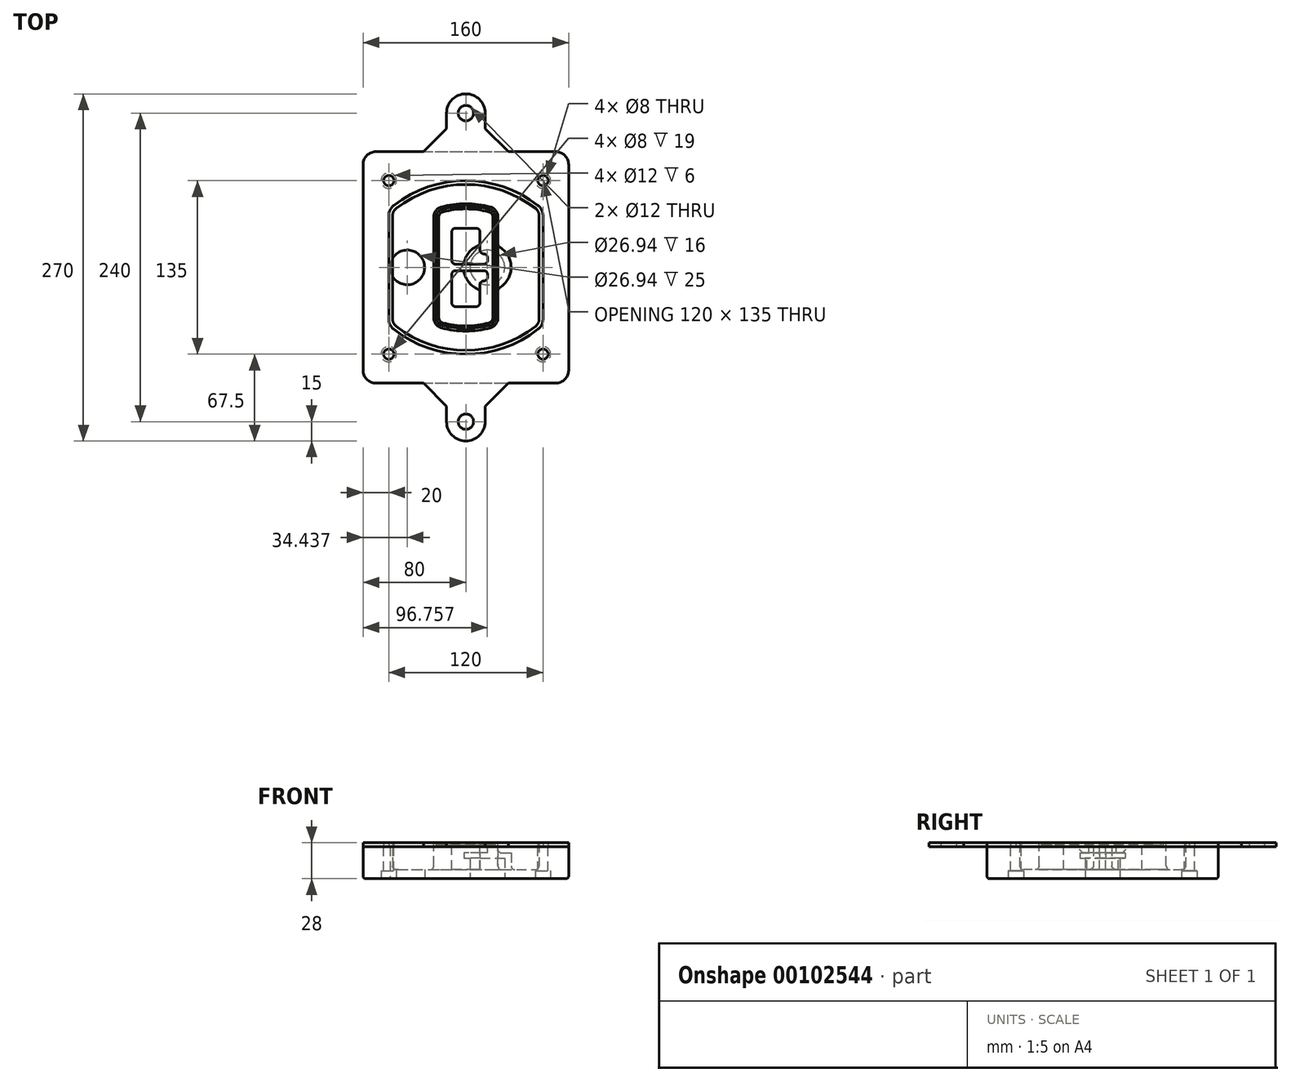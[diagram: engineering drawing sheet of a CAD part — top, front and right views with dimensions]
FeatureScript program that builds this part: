
annotation { "Feature Type Name" : "Feature", "Feature Type Description" : "" }
export const myFeature = defineFeature(function(context is Context, id is Id, definition is map)
    precondition{}
    {
        {
            var Q0;
            Q0=qCreatedBy(makeId("Top.planeOp"),FACE);
            var sketch = newSketch(context, id + "F0", { "sketchPlane" : qUnion([Q0])});
            skPoint(sketch, "E0.rect.middle", {"position": v(0, 0) * mm});
            skLineSegment(sketch, "E1.bottom", {"start": v(-70, -90) * mm, "end": v(70, -90) * mm});
            skLineSegment(sketch, "E1.top", {"start": v(-70, 90) * mm, "end": v(70, 90) * mm});
            skLineSegment(sketch, "E1.left", {"start": v(-80, -80) * mm, "end": v(-80, 80) * mm});
            skLineSegment(sketch, "E1.right", {"start": v(80, -80) * mm, "end": v(80, 80) * mm});
            skLineSegment(sketch, "E2", {"start": v(-80, 90) * mm, "end": v(80, -90) * mm, "construction": true});
            skLineSegment(sketch, "E3", {"start": v(80, 90) * mm, "end": v(-80, -90) * mm, "construction": true});
            skCircle(sketch, "E4", {"center": v(-60, 67.5) * mm, "radius": 4 * mm});
            skCircle(sketch, "E5", {"center": v(60, 67.5) * mm, "radius": 4 * mm});
            skCircle(sketch, "E6", {"center": v(60, -67.5) * mm, "radius": 4 * mm});
            skCircle(sketch, "E7", {"center": v(-60, -67.5) * mm, "radius": 4 * mm});
            skLineSegment(sketch, "E8", {"start": v(-60, 67.5) * mm, "end": v(60, 67.5) * mm, "construction": true});
            skLineSegment(sketch, "E9", {"start": v(60, 67.5) * mm, "end": v(60, -67.5) * mm, "construction": true});
            skLineSegment(sketch, "E10", {"start": v(60, -67.5) * mm, "end": v(-60, -67.5) * mm, "construction": true});
            skLineSegment(sketch, "E11", {"start": v(-60, -67.5) * mm, "end": v(-60, 67.5) * mm, "construction": true});
            skLineSegment(sketch, "E12", {"start": v(-60, 40.3) * mm, "end": v(-60, -40.3) * mm});
            skLineSegment(sketch, "E13", {"start": v(60, 40.3) * mm, "end": v(60, -40.3) * mm});
            skArc(sketch, "E14", {"start": v(56.15, 48.18) * mm, "mid": v(0, 67.5) * mm, "end": v(-56.15, 48.18) * mm});
            skArc(sketch, "E15", {"start": v(-56.15, -48.18) * mm, "mid": v(0, -67.5) * mm, "end": v(56.15, -48.18) * mm});
            skLineSegment(sketch, "E16", {"start": v(-60, 0) * mm, "end": v(60, 0) * mm, "construction": true});
            skPoint(sketch, "E17.visualSharp", {"position": v(-60, -45) * mm});
            skArc(sketch, "E17.filletArc", {"start": v(-60, -40.3) * mm, "mid": v(-58.99, -44.68) * mm, "end": v(-56.15, -48.18) * mm});
            skPoint(sketch, "E18.visualSharp", {"position": v(-60, 45) * mm});
            skArc(sketch, "E18.filletArc", {"start": v(-56.15, 48.18) * mm, "mid": v(-58.99, 44.68) * mm, "end": v(-60, 40.3) * mm});
            skPoint(sketch, "E19.visualSharp", {"position": v(60, 45) * mm});
            skArc(sketch, "E19.filletArc", {"start": v(60, 40.3) * mm, "mid": v(58.99, 44.68) * mm, "end": v(56.15, 48.18) * mm});
            skPoint(sketch, "E20.visualSharp", {"position": v(60, -45) * mm});
            skArc(sketch, "E20.filletArc", {"start": v(56.15, -48.18) * mm, "mid": v(58.99, -44.68) * mm, "end": v(60, -40.3) * mm});
            skPoint(sketch, "E21.visualSharp", {"position": v(-80, 90) * mm});
            skArc(sketch, "E21.filletArc", {"start": v(-70, 90) * mm, "mid": v(-77.07, 87.07) * mm, "end": v(-80, 80) * mm});
            skPoint(sketch, "E22.visualSharp", {"position": v(80, 90) * mm});
            skArc(sketch, "E22.filletArc", {"start": v(80, 80) * mm, "mid": v(77.07, 87.07) * mm, "end": v(70, 90) * mm});
            skPoint(sketch, "E23.visualSharp", {"position": v(80, -90) * mm});
            skArc(sketch, "E23.filletArc", {"start": v(70, -90) * mm, "mid": v(77.07, -87.07) * mm, "end": v(80, -80) * mm});
            skPoint(sketch, "E24.visualSharp", {"position": v(-80, -90) * mm});
            skArc(sketch, "E24.filletArc", {"start": v(-80, -80) * mm, "mid": v(-77.07, -87.07) * mm, "end": v(-70, -90) * mm});
            skArc(sketch, "E25.0", {"start": v(57, 40.3) * mm, "mid": v(56.3, 43.36) * mm, "end": v(54.3, 45.81) * mm});
            skLineSegment(sketch, "E25.1", {"start": v(57, 40.3) * mm, "end": v(57, -40.3) * mm});
            skArc(sketch, "E25.2", {"start": v(54.3, -45.81) * mm, "mid": v(56.3, -43.36) * mm, "end": v(57, -40.3) * mm});
            skArc(sketch, "E25.3", {"start": v(-54.3, -45.81) * mm, "mid": v(0, -64.5) * mm, "end": v(54.3, -45.81) * mm});
            skArc(sketch, "E25.4", {"start": v(-57, -40.3) * mm, "mid": v(-56.3, -43.36) * mm, "end": v(-54.3, -45.81) * mm});
            skArc(sketch, "E25.5", {"start": v(54.3, 45.81) * mm, "mid": v(0, 64.5) * mm, "end": v(-54.3, 45.81) * mm});
            skLineSegment(sketch, "E25.6", {"start": v(-57, 40.3) * mm, "end": v(-57, -40.3) * mm});
            skArc(sketch, "E25.7", {"start": v(-54.3, 45.81) * mm, "mid": v(-56.3, 43.36) * mm, "end": v(-57, 40.3) * mm});
            skArc(sketch, "E26.0", {"start": v(-58.62, 51.33) * mm, "mid": v(-62.58, 46.43) * mm, "end": v(-64, 40.3) * mm});
            skArc(sketch, "E26.1", {"start": v(58.62, 51.33) * mm, "mid": v(0, 71.5) * mm, "end": v(-58.62, 51.33) * mm});
            skArc(sketch, "E26.2", {"start": v(64, 40.3) * mm, "mid": v(62.58, 46.43) * mm, "end": v(58.62, 51.33) * mm});
            skLineSegment(sketch, "E26.3", {"start": v(64, 40.3) * mm, "end": v(64, -40.3) * mm});
            skArc(sketch, "E26.4", {"start": v(58.62, -51.33) * mm, "mid": v(62.58, -46.43) * mm, "end": v(64, -40.3) * mm});
            skLineSegment(sketch, "E26.5", {"start": v(-64, 40.3) * mm, "end": v(-64, -40.3) * mm});
            skArc(sketch, "E26.6", {"start": v(-58.62, -51.33) * mm, "mid": v(0, -71.5) * mm, "end": v(58.62, -51.33) * mm});
            skArc(sketch, "E26.7", {"start": v(-64, -40.3) * mm, "mid": v(-62.58, -46.43) * mm, "end": v(-58.62, -51.33) * mm});
            skSolve(sketch);
        }
        {
            var Q0;
            Q0=makeQuery(id+"F0.imprint","IMPRINT",FACE,{"disambiguationData":[TD([[makeQuery(id+"F0.imprint","IMPRINT",EDGE,{"derivedFrom":sQuery(id+"F0.wireOp",EDGE,"E1.bottom")}),1.0]])]});
            var Q1;
            Q1=makeQuery(id+"F0.imprint","IMPRINT",FACE,{"disambiguationData":[TD([[makeQuery(id+"F0.imprint","IMPRINT",EDGE,{"derivedFrom":sQuery(id+"F0.wireOp",EDGE,"E12")}),1.0]])]});
            var Q2;
            Q2=makeQuery(id+"F0.imprint","IMPRINT",FACE,{"disambiguationData":[TD([[makeQuery(id+"F0.imprint","IMPRINT",EDGE,{"derivedFrom":sQuery(id+"F0.wireOp",EDGE,"E25.0")}),1.0]])]});
            var Q3;
            Q3=makeQuery(id+"F0.imprint","IMPRINT",FACE,{"disambiguationData":[TD([[makeQuery(id+"F0.imprint","IMPRINT",EDGE,{"derivedFrom":sQuery(id+"F0.wireOp",EDGE,"E12")}),-1.0]])]});
            extrude(context, id + "F1", {"entities" : qUnion([Q0, Q1, Q2, Q3]), "oppositeDirection" : true, "depth" : 25 * mm});
        }
        {
            var Q0;
            Q0=makeQuery(id+"F0.imprint","IMPRINT",FACE,{"disambiguationData":[TD([[makeQuery(id+"F0.imprint","IMPRINT",EDGE,{"derivedFrom":sQuery(id+"F0.wireOp",EDGE,"E12")}),1.0]])]});
            extrude(context, id + "F2", {"entities" : qUnion([Q0]), "operationType" : NewBodyOperationType.ADD, "depth" : 3 * mm});
        }
        {
            var Q0;
            Q0=makeQuery(id+"F0.imprint","IMPRINT",FACE,{"disambiguationData":[TD([[makeQuery(id+"F0.imprint","IMPRINT",EDGE,{"derivedFrom":sQuery(id+"F0.wireOp",EDGE,"E25.0")}),1.0]])]});
            extrude(context, id + "F3", {"entities" : qUnion([Q0]), "operationType" : NewBodyOperationType.REMOVE, "oppositeDirection" : true, "depth" : 18 * mm});
        }
        {
            var Q0;
            Q0=makeQuery(id+"F2.opExtrude","CAP_FACE",FACE,{"disambiguationData":[OSD([sQuery(id+"F0.wireOp",EDGE,"E12"),sQuery(id+"F0.wireOp",EDGE,"E13"),sQuery(id+"F0.wireOp",EDGE,"E14"),sQuery(id+"F0.wireOp",EDGE,"E15"),sQuery(id+"F0.wireOp",EDGE,"E17.filletArc"),sQuery(id+"F0.wireOp",EDGE,"E18.filletArc"),sQuery(id+"F0.wireOp",EDGE,"E19.filletArc"),sQuery(id+"F0.wireOp",EDGE,"E20.filletArc"),sQuery(id+"F0.wireOp",EDGE,"E25.0"),sQuery(id+"F0.wireOp",EDGE,"E25.1"),sQuery(id+"F0.wireOp",EDGE,"E25.2"),sQuery(id+"F0.wireOp",EDGE,"E25.3"),sQuery(id+"F0.wireOp",EDGE,"E25.4"),sQuery(id+"F0.wireOp",EDGE,"E25.5"),sQuery(id+"F0.wireOp",EDGE,"E25.6"),sQuery(id+"F0.wireOp",EDGE,"E25.7")])],"isStart":false});
            var sketch = newSketch(context, id + "F4", { "sketchPlane" : qUnion([Q0])});
            skArc(sketch, "E27.0", {"start": v(-19.08, -46.97) * mm, "mid": v(0, -49.5) * mm, "end": v(19.08, -46.97) * mm});
            skArc(sketch, "E28.0", {"start": v(19.08, 46.97) * mm, "mid": v(0, 49.5) * mm, "end": v(-19.08, 46.97) * mm});
            skLineSegment(sketch, "E29", {"start": v(-25, 39.25) * mm, "end": v(-25, -39.25) * mm});
            skLineSegment(sketch, "E30", {"start": v(25, 39.25) * mm, "end": v(25, -39.25) * mm});
            skLineSegment(sketch, "E31", {"start": v(-25, 45.1) * mm, "end": v(25, 45.1) * mm, "construction": true});
            skLineSegment(sketch, "E32", {"start": v(-25, -45.1) * mm, "end": v(25, -45.1) * mm, "construction": true});
            skPoint(sketch, "E33.visualSharp", {"position": v(-25, 45.1) * mm});
            skArc(sketch, "E33.filletArc", {"start": v(-19.08, 46.97) * mm, "mid": v(-23.35, 44.11) * mm, "end": v(-25, 39.25) * mm});
            skPoint(sketch, "E34.visualSharp", {"position": v(25, 45.1) * mm});
            skArc(sketch, "E34.filletArc", {"start": v(25, 39.25) * mm, "mid": v(23.35, 44.11) * mm, "end": v(19.08, 46.97) * mm});
            skPoint(sketch, "E35.visualSharp", {"position": v(25, -45.1) * mm});
            skArc(sketch, "E35.filletArc", {"start": v(19.08, -46.97) * mm, "mid": v(23.35, -44.11) * mm, "end": v(25, -39.25) * mm});
            skPoint(sketch, "E36.visualSharp", {"position": v(-25, -45.1) * mm});
            skArc(sketch, "E36.filletArc", {"start": v(-25, -39.25) * mm, "mid": v(-23.35, -44.11) * mm, "end": v(-19.08, -46.97) * mm});
            skArc(sketch, "E37.0", {"start": v(54.3, 45.81) * mm, "mid": v(0, 64.5) * mm, "end": v(-54.3, 45.81) * mm});
            skArc(sketch, "E37.1", {"start": v(-54.3, 45.81) * mm, "mid": v(-56.3, 43.36) * mm, "end": v(-57, 40.3) * mm});
            skLineSegment(sketch, "E37.2", {"start": v(-57, 40.3) * mm, "end": v(-57, -40.3) * mm});
            skArc(sketch, "E37.3", {"start": v(-57, -40.3) * mm, "mid": v(-56.3, -43.36) * mm, "end": v(-54.3, -45.81) * mm});
            skArc(sketch, "E37.4", {"start": v(-54.3, -45.81) * mm, "mid": v(0, -64.5) * mm, "end": v(54.3, -45.81) * mm});
            skArc(sketch, "E37.5", {"start": v(54.3, -45.81) * mm, "mid": v(56.3, -43.36) * mm, "end": v(57, -40.3) * mm});
            skLineSegment(sketch, "E37.6", {"start": v(57, 40.3) * mm, "end": v(57, -40.3) * mm});
            skArc(sketch, "E37.7", {"start": v(57, 40.3) * mm, "mid": v(56.3, 43.36) * mm, "end": v(54.3, 45.81) * mm});
            skLineSegment(sketch, "E38.0", {"start": v(23, 39.25) * mm, "end": v(23, -39.25) * mm});
            skArc(sketch, "E38.1", {"start": v(18.56, -45.04) * mm, "mid": v(21.76, -42.9) * mm, "end": v(23, -39.25) * mm});
            skArc(sketch, "E38.2", {"start": v(-18.56, -45.04) * mm, "mid": v(0, -47.5) * mm, "end": v(18.56, -45.04) * mm});
            skArc(sketch, "E38.3", {"start": v(-23, -39.25) * mm, "mid": v(-21.76, -42.9) * mm, "end": v(-18.56, -45.04) * mm});
            skLineSegment(sketch, "E38.4", {"start": v(-23, 39.25) * mm, "end": v(-23, -39.25) * mm});
            skArc(sketch, "E38.5", {"start": v(23, 39.25) * mm, "mid": v(21.76, 42.9) * mm, "end": v(18.56, 45.04) * mm});
            skArc(sketch, "E38.6", {"start": v(-18.56, 45.04) * mm, "mid": v(-21.76, 42.9) * mm, "end": v(-23, 39.25) * mm});
            skArc(sketch, "E38.7", {"start": v(18.56, 45.04) * mm, "mid": v(0, 47.5) * mm, "end": v(-18.56, 45.04) * mm});
            skArc(sketch, "E39.0", {"start": v(21, 39.25) * mm, "mid": v(20.18, 41.68) * mm, "end": v(18.04, 43.1) * mm});
            skLineSegment(sketch, "E39.1", {"start": v(21, 39.25) * mm, "end": v(21, -39.25) * mm});
            skArc(sketch, "E39.2", {"start": v(18.04, -43.1) * mm, "mid": v(20.18, -41.68) * mm, "end": v(21, -39.25) * mm});
            skArc(sketch, "E39.3", {"start": v(-18.04, -43.1) * mm, "mid": v(0, -45.5) * mm, "end": v(18.04, -43.1) * mm});
            skArc(sketch, "E39.4", {"start": v(-21, -39.25) * mm, "mid": v(-20.18, -41.68) * mm, "end": v(-18.04, -43.1) * mm});
            skArc(sketch, "E39.5", {"start": v(18.04, 43.1) * mm, "mid": v(0, 45.5) * mm, "end": v(-18.04, 43.1) * mm});
            skLineSegment(sketch, "E39.6", {"start": v(-21, 39.25) * mm, "end": v(-21, -39.25) * mm});
            skArc(sketch, "E39.7", {"start": v(-18.04, 43.1) * mm, "mid": v(-20.18, 41.68) * mm, "end": v(-21, 39.25) * mm});
            skLineSegment(sketch, "E40", {"start": v(-25, 0) * mm, "end": v(25, 0) * mm, "construction": true});
            skLineSegment(sketch, "E41", {"start": v(-11, 5.5) * mm, "end": v(-11, 27.5) * mm});
            skLineSegment(sketch, "E42", {"start": v(-8, 30.5) * mm, "end": v(8, 30.5) * mm});
            skLineSegment(sketch, "E43", {"start": v(11, 27.5) * mm, "end": v(11, 13.5) * mm});
            skLineSegment(sketch, "E44", {"start": v(14, 10.5) * mm, "end": v(14, 10.5) * mm});
            skLineSegment(sketch, "E45", {"start": v(17, 7.5) * mm, "end": v(17, 5.5) * mm});
            skLineSegment(sketch, "E46", {"start": v(14, 2.5) * mm, "end": v(-8, 2.5) * mm});
            skPoint(sketch, "E47.visualSharp", {"position": v(-11, 30.5) * mm});
            skArc(sketch, "E47.filletArc", {"start": v(-8, 30.5) * mm, "mid": v(-10.12, 29.62) * mm, "end": v(-11, 27.5) * mm});
            skPoint(sketch, "E48.visualSharp", {"position": v(11, 30.5) * mm});
            skArc(sketch, "E48.filletArc", {"start": v(11, 27.5) * mm, "mid": v(10.12, 29.62) * mm, "end": v(8, 30.5) * mm});
            skPoint(sketch, "E49.visualSharp", {"position": v(11, 10.5) * mm});
            skArc(sketch, "E49.filletArc", {"start": v(11, 13.5) * mm, "mid": v(11.88, 11.38) * mm, "end": v(14, 10.5) * mm});
            skPoint(sketch, "E50.visualSharp", {"position": v(17, 10.5) * mm});
            skArc(sketch, "E50.filletArc", {"start": v(17, 7.5) * mm, "mid": v(16.12, 9.62) * mm, "end": v(14, 10.5) * mm});
            skPoint(sketch, "E51.visualSharp", {"position": v(17, 2.5) * mm});
            skArc(sketch, "E51.filletArc", {"start": v(14, 2.5) * mm, "mid": v(16.12, 3.38) * mm, "end": v(17, 5.5) * mm});
            skPoint(sketch, "E52.visualSharp", {"position": v(-11, 2.5) * mm});
            skArc(sketch, "E52.filletArc", {"start": v(-11, 5.5) * mm, "mid": v(-10.12, 3.38) * mm, "end": v(-8, 2.5) * mm});
            skLineSegment(sketch, "E53.0.MirrorCS", {"start": v(14, -2.5) * mm, "end": v(-8, -2.5) * mm});
            skArc(sketch, "E54.0.MirrorCS", {"start": v(-11, -5.5) * mm, "mid": v(-10.12, -3.38) * mm, "end": v(-8, -2.5) * mm});
            skLineSegment(sketch, "E55.0.MirrorCS", {"start": v(-11, -5.5) * mm, "end": v(-11, -27.5) * mm});
            skArc(sketch, "E56.0.MirrorCS", {"start": v(-8, -30.5) * mm, "mid": v(-10.12, -29.62) * mm, "end": v(-11, -27.5) * mm});
            skLineSegment(sketch, "E57.0.MirrorCS", {"start": v(-8, -30.5) * mm, "end": v(8, -30.5) * mm});
            skArc(sketch, "E58.0.MirrorCS", {"start": v(11, -27.5) * mm, "mid": v(10.12, -29.62) * mm, "end": v(8, -30.5) * mm});
            skLineSegment(sketch, "E59.0.MirrorCS", {"start": v(11, -27.5) * mm, "end": v(11, -13.5) * mm});
            skArc(sketch, "E60.0.MirrorCS", {"start": v(11, -13.5) * mm, "mid": v(11.88, -11.38) * mm, "end": v(14, -10.5) * mm});
            skArc(sketch, "E61.0.MirrorCS", {"start": v(17, -7.5) * mm, "mid": v(16.12, -9.62) * mm, "end": v(14, -10.5) * mm});
            skLineSegment(sketch, "E62.0.MirrorCS", {"start": v(17, -7.5) * mm, "end": v(17, -5.5) * mm});
            skArc(sketch, "E63.0.MirrorCS", {"start": v(14, -2.5) * mm, "mid": v(16.12, -3.38) * mm, "end": v(17, -5.5) * mm});
            skSolve(sketch);
        }
        {
            var Q0;
            Q0=makeQuery(id+"F4.imprint","IMPRINT",FACE,{"disambiguationData":[TD([[makeQuery(id+"F4.imprint","IMPRINT",EDGE,{"derivedFrom":sQuery(id+"F4.wireOp",EDGE,"E27.0")}),1.0]])]});
            var Q1;
            Q1=makeQuery(id+"F4.imprint","IMPRINT",FACE,{"disambiguationData":[TD([[makeQuery(id+"F4.imprint","IMPRINT",EDGE,{"derivedFrom":sQuery(id+"F4.wireOp",EDGE,"E38.0")}),-1.0]])]});
            var Q2;
            Q2=makeQuery(id+"F4.imprint","IMPRINT",FACE,{"disambiguationData":[TD([[makeQuery(id+"F4.imprint","IMPRINT",EDGE,{"derivedFrom":sQuery(id+"F4.wireOp",EDGE,"E39.0")}),1.0]])]});
            extrude(context, id + "F5", {"entities" : qUnion([Q0, Q1, Q2]), "operationType" : NewBodyOperationType.ADD, "endBound" : BoundingType.UP_TO_NEXT, "oppositeDirection" : true, "depth" : 25 * mm});
        }
        {
            var Q0;
            Q0=makeQuery(id+"F4.imprint","IMPRINT",FACE,{"disambiguationData":[TD([[makeQuery(id+"F4.imprint","IMPRINT",EDGE,{"derivedFrom":sQuery(id+"F4.wireOp",EDGE,"E38.0")}),-1.0]])]});
            extrude(context, id + "F6", {"entities" : qUnion([Q0]), "operationType" : NewBodyOperationType.REMOVE, "oppositeDirection" : true, "depth" : 2 * mm});
        }
        {
            var Q0;
            Q0=makeQuery(id+"F1.opExtrude","CAP_FACE",FACE,{"disambiguationData":[OSD([sQuery(id+"F0.wireOp",EDGE,"E1.bottom"),sQuery(id+"F0.wireOp",EDGE,"E1.top"),sQuery(id+"F0.wireOp",EDGE,"E1.left"),sQuery(id+"F0.wireOp",EDGE,"E1.right"),sQuery(id+"F0.wireOp",EDGE,"E4"),sQuery(id+"F0.wireOp",EDGE,"E5"),sQuery(id+"F0.wireOp",EDGE,"E6"),sQuery(id+"F0.wireOp",EDGE,"E7"),sQuery(id+"F0.wireOp",EDGE,"E21.filletArc"),sQuery(id+"F0.wireOp",EDGE,"E22.filletArc"),sQuery(id+"F0.wireOp",EDGE,"E23.filletArc"),sQuery(id+"F0.wireOp",EDGE,"E24.filletArc")])],"isStart":false});
            var sketch = newSketch(context, id + "F7", { "sketchPlane" : qUnion([Q0])});
            skCircle(sketch, "E64", {"center": v(16.76, 0) * mm, "radius": 13.47 * mm});
            skCircle(sketch, "E65", {"center": v(-45.56, 0) * mm, "radius": 13.47 * mm});
            skLineSegment(sketch, "E66", {"start": v(80, 0) * mm, "end": v(-80, 0) * mm});
            skCircle(sketch, "E67", {"center": v(16.76, 0) * mm, "radius": 18.47 * mm});
            skCircle(sketch, "E68", {"center": v(60, -67.5) * mm, "radius": 6 * mm});
            skCircle(sketch, "E69", {"center": v(-60, -67.5) * mm, "radius": 6 * mm});
            skCircle(sketch, "E70", {"center": v(-60, 67.5) * mm, "radius": 6 * mm});
            skCircle(sketch, "E71", {"center": v(60, 67.5) * mm, "radius": 6 * mm});
            skSolve(sketch);
        }
        {
            var Q0;
            {var subQ1=sQuery(id+"F7.wireOp",EDGE,"E66");var subQ4=sQuery(id+"F7.wireOp",EDGE,"E64");var subQ6=makeQuery(id+"F7.imprint","INTERSECT",VERTEX,{"disambiguationData":[OD(0.0)],"derivedFrom":[subQ4,subQ1]});Q0=makeQuery(id+"F7.imprint","IMPRINT",FACE,{"disambiguationData":[TD([[makeQuery(id+"F7.imprint","IMPRINT",EDGE,{"disambiguationData":[TD([[subQ6,-1.0]])],"derivedFrom":subQ4}),-1.0]])]});}
            var Q1;
            {var subQ0=sQuery(id+"F7.wireOp",EDGE,"E66");var subQ1=sQuery(id+"F7.wireOp",EDGE,"E64");var subQ3=makeQuery(id+"F7.imprint","INTERSECT",VERTEX,{"disambiguationData":[OD(0.0)],"derivedFrom":[subQ1,subQ0]});Q1=makeQuery(id+"F7.imprint","IMPRINT",FACE,{"disambiguationData":[TD([[makeQuery(id+"F7.imprint","IMPRINT",EDGE,{"disambiguationData":[TD([[subQ3,-1.0]])],"derivedFrom":subQ1}),1.0]])]});}
            var Q2;
            {var subQ0=sQuery(id+"F7.wireOp",EDGE,"E66");var subQ1=sQuery(id+"F7.wireOp",EDGE,"E64");var subQ3=makeQuery(id+"F7.imprint","INTERSECT",VERTEX,{"disambiguationData":[OD(0.0)],"derivedFrom":[subQ1,subQ0]});Q2=makeQuery(id+"F7.imprint","IMPRINT",FACE,{"disambiguationData":[TD([[makeQuery(id+"F7.imprint","IMPRINT",EDGE,{"disambiguationData":[TD([[subQ3,1.0]])],"derivedFrom":subQ1}),1.0]])]});}
            var Q3;
            {var subQ1=sQuery(id+"F7.wireOp",EDGE,"E66");var subQ4=sQuery(id+"F7.wireOp",EDGE,"E64");var subQ6=makeQuery(id+"F7.imprint","INTERSECT",VERTEX,{"disambiguationData":[OD(0.0)],"derivedFrom":[subQ4,subQ1]});Q3=makeQuery(id+"F7.imprint","IMPRINT",FACE,{"disambiguationData":[TD([[makeQuery(id+"F7.imprint","IMPRINT",EDGE,{"disambiguationData":[TD([[subQ6,1.0]])],"derivedFrom":subQ4}),-1.0]])]});}
            extrude(context, id + "F8", {"entities" : qUnion([Q0, Q1, Q2, Q3]), "operationType" : NewBodyOperationType.ADD, "oppositeDirection" : true, "depth" : 20 * mm});
        }
        {
            var Q0;
            {var subQ0=sQuery(id+"F7.wireOp",EDGE,"E66");var subQ1=sQuery(id+"F7.wireOp",EDGE,"E64");var subQ3=makeQuery(id+"F7.imprint","INTERSECT",VERTEX,{"disambiguationData":[OD(0.0)],"derivedFrom":[subQ1,subQ0]});Q0=makeQuery(id+"F7.imprint","IMPRINT",FACE,{"disambiguationData":[TD([[makeQuery(id+"F7.imprint","IMPRINT",EDGE,{"disambiguationData":[TD([[subQ3,-1.0]])],"derivedFrom":subQ1}),1.0]])]});}
            var Q1;
            {var subQ0=sQuery(id+"F7.wireOp",EDGE,"E66");var subQ1=sQuery(id+"F7.wireOp",EDGE,"E64");var subQ3=makeQuery(id+"F7.imprint","INTERSECT",VERTEX,{"disambiguationData":[OD(0.0)],"derivedFrom":[subQ1,subQ0]});Q1=makeQuery(id+"F7.imprint","IMPRINT",FACE,{"disambiguationData":[TD([[makeQuery(id+"F7.imprint","IMPRINT",EDGE,{"disambiguationData":[TD([[subQ3,1.0]])],"derivedFrom":subQ1}),1.0]])]});}
            extrude(context, id + "F9", {"entities" : qUnion([Q0, Q1]), "operationType" : NewBodyOperationType.REMOVE, "oppositeDirection" : true, "depth" : 16 * mm});
        }
        {
            var Q0;
            {var subQ0=sQuery(id+"F7.wireOp",EDGE,"E66");var subQ1=sQuery(id+"F7.wireOp",EDGE,"E65");var subQ3=makeQuery(id+"F7.imprint","INTERSECT",VERTEX,{"disambiguationData":[OD(0.0)],"derivedFrom":[subQ1,subQ0]});Q0=makeQuery(id+"F7.imprint","IMPRINT",FACE,{"disambiguationData":[TD([[makeQuery(id+"F7.imprint","IMPRINT",EDGE,{"disambiguationData":[TD([[subQ3,-1.0]])],"derivedFrom":subQ1}),1.0]])]});}
            var Q1;
            {var subQ0=sQuery(id+"F7.wireOp",EDGE,"E66");var subQ1=sQuery(id+"F7.wireOp",EDGE,"E65");var subQ3=makeQuery(id+"F7.imprint","INTERSECT",VERTEX,{"disambiguationData":[OD(0.0)],"derivedFrom":[subQ1,subQ0]});Q1=makeQuery(id+"F7.imprint","IMPRINT",FACE,{"disambiguationData":[TD([[makeQuery(id+"F7.imprint","IMPRINT",EDGE,{"disambiguationData":[TD([[subQ3,1.0]])],"derivedFrom":subQ1}),1.0]])]});}
            extrude(context, id + "F10", {"entities" : qUnion([Q0, Q1]), "operationType" : NewBodyOperationType.REMOVE, "oppositeDirection" : true, "depth" : 25 * mm});
        }
        {
            var Q0;
            Q0=makeQuery(id+"F7.imprint","IMPRINT",FACE,{"disambiguationData":[TD([[makeQuery(id+"F7.imprint","IMPRINT",EDGE,{"derivedFrom":sQuery(id+"F7.wireOp",EDGE,"E68")}),1.0]])]});
            var Q1;
            Q1=makeQuery(id+"F7.imprint","IMPRINT",FACE,{"disambiguationData":[TD([[makeQuery(id+"F7.imprint","IMPRINT",EDGE,{"derivedFrom":makeQuery(id+"F1.opExtrude","CAP_EDGE",EDGE,{"disambiguationData":[OSD([sQuery(id+"F0.wireOp",EDGE,"E5")])],"isStart":false})}),-1.0]])]});
            var Q2;
            Q2=makeQuery(id+"F7.imprint","IMPRINT",FACE,{"disambiguationData":[TD([[makeQuery(id+"F7.imprint","IMPRINT",EDGE,{"derivedFrom":sQuery(id+"F7.wireOp",EDGE,"E69")}),1.0]])]});
            var Q3;
            Q3=makeQuery(id+"F7.imprint","IMPRINT",FACE,{"disambiguationData":[TD([[makeQuery(id+"F7.imprint","IMPRINT",EDGE,{"derivedFrom":makeQuery(id+"F1.opExtrude","CAP_EDGE",EDGE,{"disambiguationData":[OSD([sQuery(id+"F0.wireOp",EDGE,"E4")])],"isStart":false})}),-1.0]])]});
            var Q4;
            Q4=makeQuery(id+"F7.imprint","IMPRINT",FACE,{"disambiguationData":[TD([[makeQuery(id+"F7.imprint","IMPRINT",EDGE,{"derivedFrom":sQuery(id+"F7.wireOp",EDGE,"E70")}),1.0]])]});
            var Q5;
            Q5=makeQuery(id+"F7.imprint","IMPRINT",FACE,{"disambiguationData":[TD([[makeQuery(id+"F7.imprint","IMPRINT",EDGE,{"derivedFrom":makeQuery(id+"F1.opExtrude","CAP_EDGE",EDGE,{"disambiguationData":[OSD([sQuery(id+"F0.wireOp",EDGE,"E7")])],"isStart":false})}),-1.0]])]});
            var Q6;
            Q6=makeQuery(id+"F7.imprint","IMPRINT",FACE,{"disambiguationData":[TD([[makeQuery(id+"F7.imprint","IMPRINT",EDGE,{"derivedFrom":sQuery(id+"F7.wireOp",EDGE,"E71")}),1.0]])]});
            var Q7;
            Q7=makeQuery(id+"F7.imprint","IMPRINT",FACE,{"disambiguationData":[TD([[makeQuery(id+"F7.imprint","IMPRINT",EDGE,{"derivedFrom":makeQuery(id+"F1.opExtrude","CAP_EDGE",EDGE,{"disambiguationData":[OSD([sQuery(id+"F0.wireOp",EDGE,"E6")])],"isStart":false})}),-1.0]])]});
            extrude(context, id + "F11", {"entities" : qUnion([Q0, Q1, Q2, Q3, Q4, Q5, Q6, Q7]), "operationType" : NewBodyOperationType.REMOVE, "oppositeDirection" : true, "depth" : 6 * mm});
        }
        {
            var Q0;
            Q0=makeQuery(id+"F9.boolean.opBoolean","COPY",FACE,{"derivedFrom":makeQuery(id+"F9.opExtrude","CAP_FACE",FACE,{"disambiguationData":[OSD([sQuery(id+"F7.wireOp",EDGE,"E64")])],"isStart":false})});
            var sketch = newSketch(context, id + "F12", { "sketchPlane" : qUnion([Q0])});
            skArc(sketch, "E72.0", {"start": v(11, 17.55) * mm, "mid": v(2.57, 11.82) * mm, "end": v(-1.54, 2.5) * mm});
            skArc(sketch, "E72.1", {"start": v(-1.54, -2.5) * mm, "mid": v(2.57, -11.82) * mm, "end": v(11, -17.55) * mm});
            skLineSegment(sketch, "E73", {"start": v(-1.54, -2.5) * mm, "end": v(14, -2.5) * mm});
            skLineSegment(sketch, "E74.0", {"start": v(14, 2.5) * mm, "end": v(-1.54, 2.5) * mm});
            skArc(sketch, "E74.1", {"start": v(14, 2.5) * mm, "mid": v(16.12, 3.38) * mm, "end": v(17, 5.5) * mm});
            skLineSegment(sketch, "E74.2", {"start": v(17, 7.5) * mm, "end": v(17, 5.5) * mm});
            skArc(sketch, "E74.3", {"start": v(17, 7.5) * mm, "mid": v(16.12, 9.62) * mm, "end": v(14, 10.5) * mm});
            skArc(sketch, "E74.4", {"start": v(11, 13.5) * mm, "mid": v(11.88, 11.38) * mm, "end": v(14, 10.5) * mm});
            skLineSegment(sketch, "E74.5", {"start": v(11, 17.55) * mm, "end": v(11, 13.5) * mm});
            skLineSegment(sketch, "E74.7", {"start": v(14, -2.5) * mm, "end": v(-1.54, -2.5) * mm});
            skArc(sketch, "E74.8", {"start": v(14, -2.5) * mm, "mid": v(16.12, -3.38) * mm, "end": v(17, -5.5) * mm});
            skLineSegment(sketch, "E74.9", {"start": v(17, -7.5) * mm, "end": v(17, -5.5) * mm});
            skArc(sketch, "E74.10", {"start": v(17, -7.5) * mm, "mid": v(16.12, -9.62) * mm, "end": v(14, -10.5) * mm});
            skArc(sketch, "E74.11", {"start": v(11, -13.5) * mm, "mid": v(11.88, -11.38) * mm, "end": v(14, -10.5) * mm});
            skLineSegment(sketch, "E74.12", {"start": v(11, -17.55) * mm, "end": v(11, -13.5) * mm});
            skPoint(sketch, "E75.orphan", {"position": v(11, -27.5) * mm});
            skPoint(sketch, "E76.orphan", {"position": v(-8, -2.5) * mm});
            skPoint(sketch, "E77.orphan", {"position": v(-8, 2.5) * mm});
            skPoint(sketch, "E78.orphan", {"position": v(11, 27.5) * mm});
            skSolve(sketch);
        }
        {
            var Q0;
            {var subQ7=sQuery(id+"F12.wireOp",EDGE,"E72.0");var subQ14=sQuery(id+"F12.wireOp",EDGE,"E72.1");var subQ16=sQuery(id+"F12.wireOp",EDGE,"E74.1");var subQ18=sQuery(id+"F12.wireOp",EDGE,"E74.8");Q0=qUnion([makeQuery(id+"F12.imprint","IMPRINT",FACE,{"disambiguationData":[TD([[makeQuery(id+"F12.imprint","IMPRINT",EDGE,{"derivedFrom":subQ7}),1.0]])]}),makeQuery(id+"F12.imprint","IMPRINT",FACE,{"disambiguationData":[TD([[makeQuery(id+"F12.imprint","IMPRINT",EDGE,{"derivedFrom":subQ14}),1.0]])]}),makeQuery(id+"F12.imprint","IMPRINT",FACE,{"disambiguationData":[TD([[makeQuery(id+"F12.imprint","IMPRINT",EDGE,{"derivedFrom":subQ16}),1.0]])]}),makeQuery(id+"F12.imprint","IMPRINT",FACE,{"disambiguationData":[TD([[makeQuery(id+"F12.imprint","IMPRINT",EDGE,{"derivedFrom":subQ18}),-1.0]])]})]);}
            var Q1;
            Q1=makeQuery(id+"F5.boolean.opBoolean","SPLIT",FACE,{"disambiguationData":[TD([makeQuery(id+"F5.opExtrude","SWEPT_FACE",FACE,{"disambiguationData":[OSD([sQuery(id+"F4.wireOp",EDGE,"E41")])]})])],"derivedFrom":makeQuery(id+"F3.boolean.opBoolean","COPY",FACE,{"derivedFrom":makeQuery(id+"F3.opExtrude","CAP_FACE",FACE,{"disambiguationData":[OSD([sQuery(id+"F0.wireOp",EDGE,"E25.0"),sQuery(id+"F0.wireOp",EDGE,"E25.1"),sQuery(id+"F0.wireOp",EDGE,"E25.2"),sQuery(id+"F0.wireOp",EDGE,"E25.3"),sQuery(id+"F0.wireOp",EDGE,"E25.4"),sQuery(id+"F0.wireOp",EDGE,"E25.5"),sQuery(id+"F0.wireOp",EDGE,"E25.6"),sQuery(id+"F0.wireOp",EDGE,"E25.7")])],"isStart":false})})});
            extrude(context, id + "F13", {"entities" : qUnion([Q0]), "operationType" : NewBodyOperationType.REMOVE, "endBound" : BoundingType.UP_TO_SURFACE, "endBoundEntityFace" : qUnion([Q1]), "depth" : 25 * mm});
        }
        {
            var Q0;
            Q0=makeQuery(id+"F3.boolean.opBoolean","COPY",EDGE,{"derivedFrom":makeQuery(id+"F3.opExtrude","CAP_EDGE",EDGE,{"disambiguationData":[OSD([sQuery(id+"F0.wireOp",EDGE,"E25.6")])],"isStart":false})});
            var Q1;
            Q1=makeQuery(id+"F8.boolean.opBoolean","INTERSECT",EDGE,{"derivedFrom":[makeQuery(id+"F5.opExtrude","SWEPT_FACE",FACE,{"disambiguationData":[OSD([sQuery(id+"F4.wireOp",EDGE,"E30")])]}),makeQuery(id+"F8.opExtrude","CAP_FACE",FACE,{"disambiguationData":[OSD([sQuery(id+"F7.wireOp",EDGE,"E67")])],"isStart":false})]});
            var Q2;
            Q2=makeQuery(id+"F8.boolean.opBoolean","INTERSECT",EDGE,{"disambiguationData":[OD(1.0)],"derivedFrom":[makeQuery(id+"F5.opExtrude","SWEPT_FACE",FACE,{"disambiguationData":[OSD([sQuery(id+"F4.wireOp",EDGE,"E30")])]}),makeQuery(id+"F8.opExtrude","SWEPT_FACE",FACE,{"disambiguationData":[OSD([sQuery(id+"F7.wireOp",EDGE,"E67")])]})]});
            var Q3;
            {var subQ0=sQuery(id+"F4.wireOp",EDGE,"E30");Q3=makeQuery(id+"F8.boolean.opBoolean","SPLIT",EDGE,{"disambiguationData":[TD([makeQuery(id+"F5.opExtrude","SWEPT_FACE",FACE,{"disambiguationData":[OSD([sQuery(id+"F4.wireOp",EDGE,"E35.filletArc")])]})])],"derivedFrom":makeQuery(id+"F5.opExtrude","CAP_EDGE",EDGE,{"disambiguationData":[OSD([subQ0])],"isStart":false})});}
            var Q4;
            {var subQ0=sQuery(id+"F0.wireOp",EDGE,"E25.7");var subQ1=sQuery(id+"F0.wireOp",EDGE,"E25.1");var subQ2=sQuery(id+"F0.wireOp",EDGE,"E25.6");var subQ3=sQuery(id+"F0.wireOp",EDGE,"E25.5");var subQ4=sQuery(id+"F0.wireOp",EDGE,"E25.4");var subQ5=sQuery(id+"F0.wireOp",EDGE,"E25.0");var subQ6=sQuery(id+"F0.wireOp",EDGE,"E25.2");var subQ7=sQuery(id+"F0.wireOp",EDGE,"E25.3");Q4=makeQuery(id+"F8.boolean.opBoolean","INTERSECT",EDGE,{"derivedFrom":[makeQuery(id+"F5.boolean.opBoolean","SPLIT",FACE,{"disambiguationData":[TD([makeQuery(id+"F2.opExtrude","SWEPT_FACE",FACE,{"disambiguationData":[OSD([subQ5])]})])],"derivedFrom":makeQuery(id+"F3.boolean.opBoolean","COPY",FACE,{"derivedFrom":makeQuery(id+"F3.opExtrude","CAP_FACE",FACE,{"disambiguationData":[OSD([subQ5,subQ1,subQ6,subQ7,subQ4,subQ3,subQ2,subQ0])],"isStart":false})})}),makeQuery(id+"F8.opExtrude","SWEPT_FACE",FACE,{"disambiguationData":[OSD([sQuery(id+"F7.wireOp",EDGE,"E67")])]})]});}
            var Q5;
            Q5=makeQuery(id+"F8.boolean.opBoolean","INTERSECT",EDGE,{"disambiguationData":[OD(0.0)],"derivedFrom":[makeQuery(id+"F5.opExtrude","SWEPT_FACE",FACE,{"disambiguationData":[OSD([sQuery(id+"F4.wireOp",EDGE,"E30")])]}),makeQuery(id+"F8.opExtrude","SWEPT_FACE",FACE,{"disambiguationData":[OSD([sQuery(id+"F7.wireOp",EDGE,"E67")])]})]});
            fillet(context, id + "F14", {"entities" : qUnion([Q0, Q1, Q2, Q3, Q4, Q5]), "radius" : 3 * mm, "tangentPropagation" : true, "allowEdgeOverflow" : false});
        }
        {
            var Q0;
            Q0=makeQuery(id+"F1.opExtrude","CAP_EDGE",EDGE,{"disambiguationData":[OSD([sQuery(id+"F0.wireOp",EDGE,"E1.bottom")])],"isStart":false});
            fillet(context, id + "F15", {"entities" : qUnion([Q0]), "radius" : 2 * mm, "tangentPropagation" : true, "allowEdgeOverflow" : false});
        }
        {
            var Q0;
            {var subQ0=sQuery(id+"F0.wireOp",EDGE,"E22.filletArc");var subQ1=sQuery(id+"F0.wireOp",EDGE,"E7");var subQ2=sQuery(id+"F0.wireOp",EDGE,"E6");var subQ3=sQuery(id+"F0.wireOp",EDGE,"E5");var subQ4=sQuery(id+"F0.wireOp",EDGE,"E4");var subQ5=sQuery(id+"F0.wireOp",EDGE,"E1.bottom");var subQ6=sQuery(id+"F0.wireOp",EDGE,"E21.filletArc");var subQ7=sQuery(id+"F0.wireOp",EDGE,"E1.top");var subQ8=sQuery(id+"F0.wireOp",EDGE,"E1.left");var subQ9=sQuery(id+"F0.wireOp",EDGE,"E1.right");var subQ10=sQuery(id+"F0.wireOp",EDGE,"E23.filletArc");var subQ11=sQuery(id+"F0.wireOp",EDGE,"E24.filletArc");Q0=makeQuery(id+"F2.boolean.opBoolean","SPLIT",FACE,{"disambiguationData":[TD([makeQuery(id+"F1.opExtrude","SWEPT_FACE",FACE,{"disambiguationData":[OSD([subQ5])]})])],"derivedFrom":makeQuery(id+"F1.opExtrude","CAP_FACE",FACE,{"disambiguationData":[OSD([subQ5,subQ7,subQ8,subQ9,subQ4,subQ3,subQ2,subQ1,subQ6,subQ0,subQ10,subQ11])],"isStart":true})});}
            var sketch = newSketch(context, id + "F16", { "sketchPlane" : qUnion([Q0])});
            skLineSegment(sketch, "E79", {"start": v(0, 90) * mm, "end": v(0, 120) * mm, "construction": true});
            skCircle(sketch, "E80", {"center": v(0, 120) * mm, "radius": 6 * mm});
            skLineSegment(sketch, "E81", {"start": v(-15, 108) * mm, "end": v(-33, 90) * mm});
            skLineSegment(sketch, "E82", {"start": v(-15, 108) * mm, "end": v(-15, 120) * mm});
            skArc(sketch, "E83", {"start": v(15, 120) * mm, "mid": v(0, 135) * mm, "end": v(-15, 120) * mm});
            skLineSegment(sketch, "E84", {"start": v(15, 120) * mm, "end": v(15, 108) * mm});
            skLineSegment(sketch, "E85", {"start": v(15, 108) * mm, "end": v(33, 90) * mm});
            skLineSegment(sketch, "E86", {"start": v(-80, 0) * mm, "end": v(80, 0) * mm, "construction": true});
            skLineSegment(sketch, "E87.MirrorCS", {"start": v(-15, -108) * mm, "end": v(-33, -90) * mm});
            skLineSegment(sketch, "E88.MirrorCS", {"start": v(-15, -108) * mm, "end": v(-15, -120) * mm});
            skArc(sketch, "E89.MirrorCS", {"start": v(15, -120) * mm, "mid": v(0, -135) * mm, "end": v(-15, -120) * mm});
            skLineSegment(sketch, "E90.MirrorCS", {"start": v(15, -120) * mm, "end": v(15, -108) * mm});
            skLineSegment(sketch, "E91.MirrorCS", {"start": v(15, -108) * mm, "end": v(33, -90) * mm});
            skCircle(sketch, "E92.MirrorC", {"center": v(0, -120) * mm, "radius": 6 * mm});
            skLineSegment(sketch, "E93.MirrorCS", {"start": v(0, -90) * mm, "end": v(0, -120) * mm, "construction": true});
            skSolve(sketch);
        }
        {
            var Q0;
            Q0=makeQuery(id+"F16.imprint","IMPRINT",FACE,{"disambiguationData":[TD([[makeQuery(id+"F16.imprint","IMPRINT",EDGE,{"derivedFrom":sQuery(id+"F16.wireOp",EDGE,"E80")}),-1.0]])]});
            var Q1;
            {var subQ0=sQuery(id+"F16.wireOp",EDGE,"E87.MirrorCS");Q1=makeQuery(id+"F16.imprint","IMPRINT",FACE,{"disambiguationData":[TD([[makeQuery(id+"F16.imprint","IMPRINT",EDGE,{"derivedFrom":subQ0}),-1.0]])]});}
            var Q2;
            Q2=makeQuery(id+"F16.imprint","IMPRINT",FACE,{"disambiguationData":[TD([[makeQuery(id+"F16.imprint","IMPRINT",EDGE,{"derivedFrom":makeQuery(id+"F1.opExtrude","CAP_EDGE",EDGE,{"disambiguationData":[OSD([sQuery(id+"F0.wireOp",EDGE,"E4")])],"isStart":true})}),-1.0]])]});
            var Q3;
            Q3=makeQuery(id+"F16.imprint","IMPRINT",FACE,{"disambiguationData":[TD([[makeQuery(id+"F16.imprint","IMPRINT",EDGE,{"derivedFrom":makeQuery(id+"F1.opExtrude","CAP_EDGE",EDGE,{"disambiguationData":[OSD([sQuery(id+"F0.wireOp",EDGE,"E6")])],"isStart":true})}),-1.0]])]});
            var Q4;
            Q4=makeQuery(id+"F2.opExtrude","CAP_FACE",FACE,{"disambiguationData":[OSD([sQuery(id+"F0.wireOp",EDGE,"E12"),sQuery(id+"F0.wireOp",EDGE,"E13"),sQuery(id+"F0.wireOp",EDGE,"E14"),sQuery(id+"F0.wireOp",EDGE,"E15"),sQuery(id+"F0.wireOp",EDGE,"E17.filletArc"),sQuery(id+"F0.wireOp",EDGE,"E18.filletArc"),sQuery(id+"F0.wireOp",EDGE,"E19.filletArc"),sQuery(id+"F0.wireOp",EDGE,"E20.filletArc"),sQuery(id+"F0.wireOp",EDGE,"E25.0"),sQuery(id+"F0.wireOp",EDGE,"E25.1"),sQuery(id+"F0.wireOp",EDGE,"E25.2"),sQuery(id+"F0.wireOp",EDGE,"E25.3"),sQuery(id+"F0.wireOp",EDGE,"E25.4"),sQuery(id+"F0.wireOp",EDGE,"E25.5"),sQuery(id+"F0.wireOp",EDGE,"E25.6"),sQuery(id+"F0.wireOp",EDGE,"E25.7")])],"isStart":false});
            extrude(context, id + "F17", {"entities" : qUnion([Q0, Q1, Q2, Q3]), "endBound" : BoundingType.UP_TO_SURFACE, "endBoundEntityFace" : qUnion([Q4]), "depth" : 25 * mm});
        }
    });
